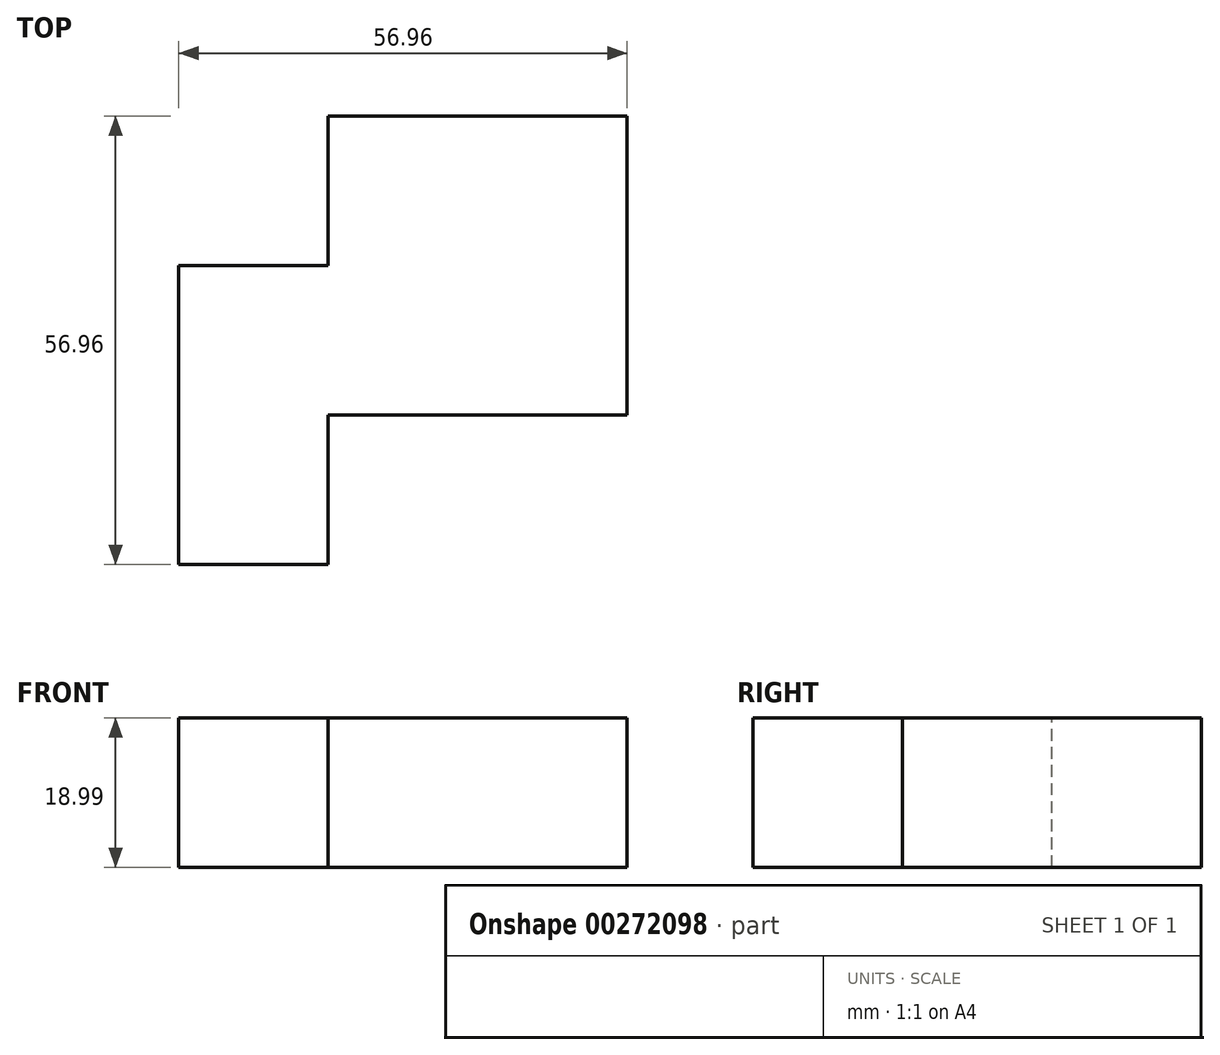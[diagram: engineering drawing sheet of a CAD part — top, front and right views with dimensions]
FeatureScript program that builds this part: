
annotation { "Feature Type Name" : "Feature", "Feature Type Description" : "" }
export const myFeature = defineFeature(function(context is Context, id is Id, definition is map)
    precondition{}
    {
        {
            var Q0;
            Q0=qCreatedBy(makeId("Top.planeOp"),FACE);
            var sketch = newSketch(context, id + "F0", { "sketchPlane" : qUnion([Q0])});
            skLineSegment(sketch, "E0.bottom", {"start": v(-18.99, 18.99) * mm, "end": v(18.99, 18.99) * mm});
            skLineSegment(sketch, "E0.top", {"start": v(-18.99, -18.99) * mm, "end": v(18.99, -18.99) * mm});
            skLineSegment(sketch, "E0.left", {"start": v(-18.99, 18.99) * mm, "end": v(-18.99, -18.99) * mm});
            skLineSegment(sketch, "E0.right", {"start": v(18.99, 18.99) * mm, "end": v(18.99, -18.99) * mm});
            skPoint(sketch, "E0.middle", {"position": v(0, 0) * mm});
            skSolve(sketch);
        }
        {
            var Q0;
            Q0=makeQuery(id+"F0.imprint","IMPRINT",FACE,{"disambiguationData":[TD([[makeQuery(id+"F0.imprint","IMPRINT",EDGE,{"derivedFrom":sQuery(id+"F0.wireOp",EDGE,"E0.bottom")}),-1.0]])]});
            extrude(context, id + "F1", {"entities" : qUnion([Q0]), "depth" : 18.99 * mm});
        }
        {
            var Q0;
            Q0=makeQuery(id+"F1.opExtrude","CAP_FACE",FACE,{"disambiguationData":[OSD([sQuery(id+"F0.wireOp",EDGE,"E0.bottom"),sQuery(id+"F0.wireOp",EDGE,"E0.top"),sQuery(id+"F0.wireOp",EDGE,"E0.left"),sQuery(id+"F0.wireOp",EDGE,"E0.right")])],"isStart":false});
            var sketch = newSketch(context, id + "F2", { "sketchPlane" : qUnion([Q0])});
            skLineSegment(sketch, "E1.bottom", {"start": v(-18.99, 0) * mm, "end": v(-37.97, 0) * mm});
            skLineSegment(sketch, "E1.top", {"start": v(-18.99, -37.97) * mm, "end": v(-37.97, -37.97) * mm});
            skLineSegment(sketch, "E1.left", {"start": v(-18.99, 0) * mm, "end": v(-18.99, -37.97) * mm});
            skLineSegment(sketch, "E1.right", {"start": v(-37.97, 0) * mm, "end": v(-37.97, -37.97) * mm});
            skSolve(sketch);
        }
        {
            var Q0;
            Q0 = qSketchRegion(id + "F2", true);
            extrude(context, id + "F3", {"entities" : qUnion([Q0]), "operationType" : NewBodyOperationType.ADD, "oppositeDirection" : true, "depth" : 18.99 * mm});
        }
    });
